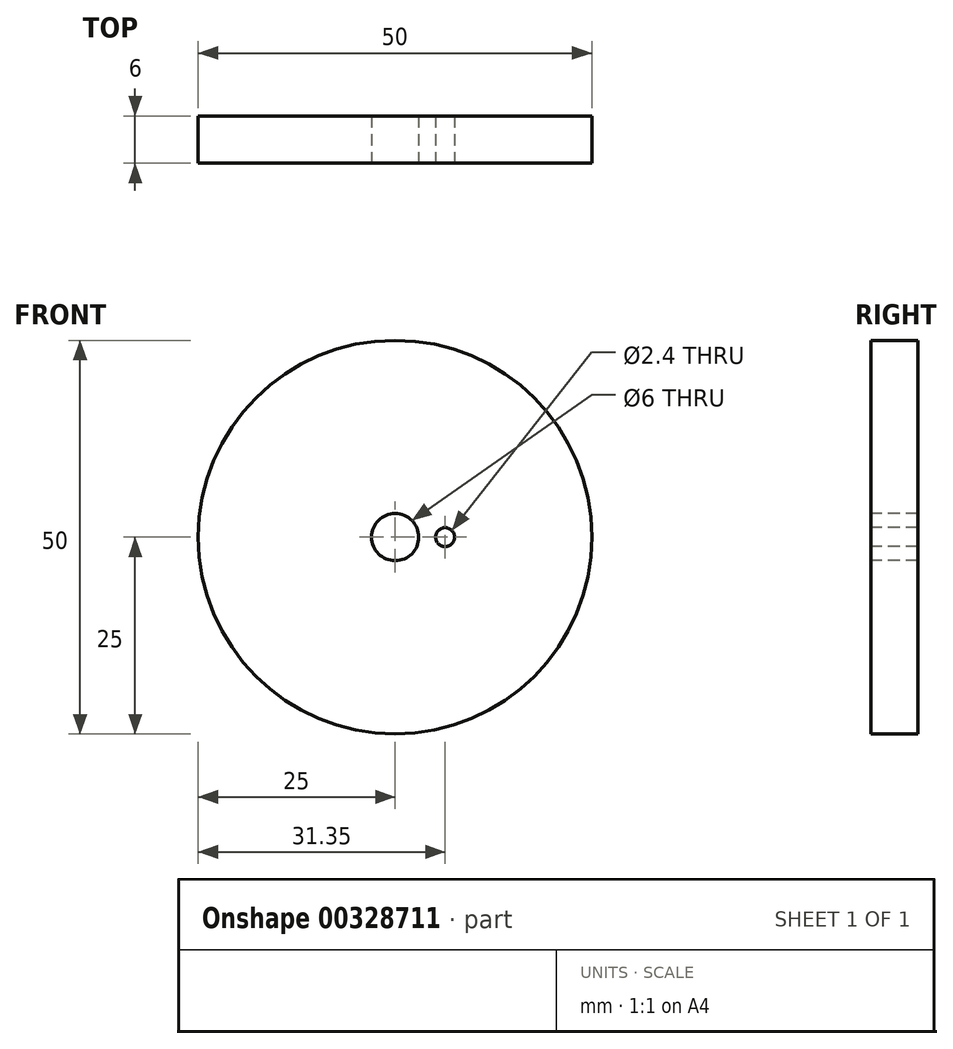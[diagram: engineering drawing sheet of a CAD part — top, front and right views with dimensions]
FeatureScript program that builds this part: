
annotation { "Feature Type Name" : "Feature", "Feature Type Description" : "" }
export const myFeature = defineFeature(function(context is Context, id is Id, definition is map)
    precondition{}
    {
        {
            var Q0;
            Q0=qCreatedBy(makeId("Front.planeOp"),FACE);
            var sketch = newSketch(context, id + "F0", { "sketchPlane" : qUnion([Q0])});
            skCircle(sketch, "E0", {"center": v(0, 0) * mm, "radius": 25 * mm});
            skSolve(sketch);
        }
        {
            var Q0;
            Q0 = qSketchRegion(id + "F0", true);
            extrude(context, id + "F1", {"entities" : qUnion([Q0]), "depth" : 3 * mm, "hasSecondDirection" : true, "secondDirectionOppositeDirection" : true, "secondDirectionDepth" : 3 * mm});
        }
        {
            var Q0;
            Q0=makeQuery(id+"F1.opExtrude","CAP_FACE",FACE,{"disambiguationData":[OSD([sQuery(id+"F0.wireOp",EDGE,"E0")])],"isStart":false});
            var sketch = newSketch(context, id + "F2", { "sketchPlane" : qUnion([Q0])});
            skCircle(sketch, "E1", {"center": v(0, 0) * mm, "radius": 3 * mm});
            skCircle(sketch, "E2", {"center": v(6.35, 0) * mm, "radius": 1.2 * mm});
            skSolve(sketch);
        }
        {
            var Q0;
            Q0 = qSketchRegion(id + "F2", true);
            extrude(context, id + "F3", {"entities" : qUnion([Q0]), "operationType" : NewBodyOperationType.REMOVE, "endBound" : BoundingType.THROUGH_ALL, "oppositeDirection" : true, "depth" : 25 * mm});
        }
    });
